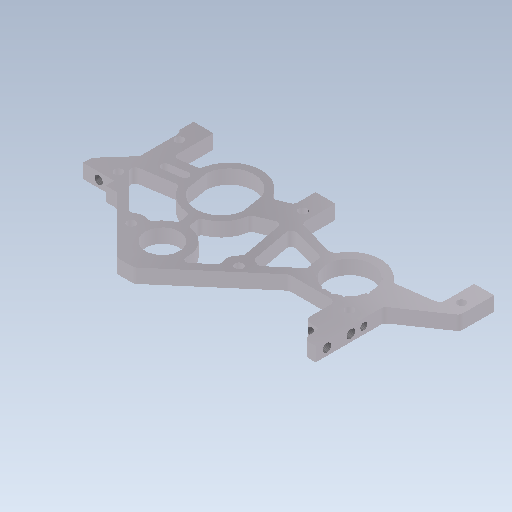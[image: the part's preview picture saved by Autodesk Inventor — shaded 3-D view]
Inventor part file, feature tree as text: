
AUTODESK INVENTOR PART (.ipt)
format: ipt  version: 2020 (Build 240168000, 168)  size: 420,864 bytes
history: native  units: mm
features: sketch x26, extrude x9, hole x9, thread x7, fillet x2, plane x1
ambient origin geometry x8: Origin, YZ Plane, XZ Plane, XY Plane, X Axis, Y Axis, Z Axis, Center Point
bodies: Solid1 (feature_tree)
feature tree (54):
  plane  "Work Plane1"
  extrude  "Extrude8"  Depth=5.0mm
  fillet  "Fillet1"  Radius=2.0mm
  extrude  "Extrude7"  Depth=2.0mm
  extrude  "Extrude6"  Depth=2.0mm
  extrude  "Extrude5"  Depth=2.0mm
  extrude  "Extrude4"  Depth=2.0mm
  extrude  "Extrude3"  Depth=1.5mm
  extrude  "Extrude2"  Depth=1.5mm
  extrude  "Extrude1"  Depth=2.0mm
  hole  "Hole8"  [1 undecoded]
  hole  "Hole7"  [1 undecoded]
  hole  "Hole6"  [1 undecoded]
  hole  "Hole5"  [1 undecoded]
  hole  "Hole4"  [1 undecoded]
  hole  "Hole3"  [1 undecoded]
  hole  "Hole2"  [1 undecoded]
  hole  "Hole1"  [1 undecoded]
  thread  "Thread1"  [1 undecoded]
  thread  "Thread2"  [1 undecoded]
  thread  "Thread3"  [1 undecoded]
  thread  "Thread4"  [1 undecoded]
  thread  "Thread5"  [1 undecoded]
  thread  "Thread6"  [1 undecoded]
  thread  "Thread7"  [1 undecoded]
  hole  "Hole23"  [1 undecoded]
  extrude  "Extrusion11"  [1 undecoded]
  fillet  "Fillet2"  [1 undecoded]
  sketch  "Sketch25"  dims[d99=3.0mm d100=6.0mm d101=4.0mm d102=2.0mm d103=90.0deg d104=8.0mm d105=20.594885mm]
  sketch  "Sketch1"  dims[d0=21.5mm d1=5.0mm d2=0.0mm d3=2.0mm]
  sketch  "Sketch2"  dims[d4=2.0mm d5=2.0mm]
  sketch  "Sketch3"  dims[d6=2.0mm d7=2.0mm]
  sketch  "Sketch4"  dims[d8=2.0mm d9=2.0mm]
  sketch  "Sketch5"  dims[d10=2.0mm d11=2.0mm]
  sketch  "Sketch6"  dims[d12=1.5mm d13=1.5mm]
  sketch  "Sketch7"  dims[d14=1.5mm d15=1.5mm]
  sketch  "Sketch8"  dims[d16=2.0mm d17=2.0mm]
  sketch  "Sketch9"  dims[d18=2.0mm d19=2.0mm]
  sketch  "Sketch10"  dims[d20=2.0mm d21=2.0mm]
  sketch  "Sketch11"  dims[d22=3.0mm d23=-0.0mm d24=5.0mm d25=-0.0mm]
  sketch  "Sketch12"  dims[d26=5.0mm d27=-0.0mm d28=5.0mm d29=-0.0mm]
  sketch  "Sketch13"  dims[d30=5.0mm d31=-0.0mm d32=5.0mm d33=-0.0mm]
  sketch  "Sketch14"  dims[d34=5.0mm d35=-0.0mm]
  sketch  "Sketch15"  dims[d36=3.0mm d37=6.0mm d38=4.0mm d39=2.0mm d40=90.0deg d41=6.0mm d42=20.594885mm]
  sketch  "Sketch16"  dims[d43=3.0mm d44=6.0mm d45=4.0mm d46=2.0mm d47=90.0deg d48=4.0mm d49=20.594885mm]
  sketch  "Sketch17"  dims[d50=3.0mm d51=6.0mm d52=4.0mm d53=2.0mm d54=90.0deg d55=8.0mm d56=20.594885mm]
  sketch  "Sketch18"  dims[d57=3.0mm d58=6.0mm d59=4.0mm d60=2.0mm d61=90.0deg d62=8.0mm d63=20.594885mm]
  sketch  "Sketch19"  dims[d64=3.0mm d65=6.0mm d66=4.0mm d67=2.0mm d68=90.0deg d69=8.0mm d70=20.594885mm]
  sketch  "Sketch20"  dims[d71=3.0mm d72=6.0mm d73=4.0mm d74=2.0mm d75=90.0deg d76=8.0mm d77=20.594885mm]
  sketch  "Sketch21"  dims[d78=3.0mm d79=6.0mm d80=4.0mm d81=2.0mm d82=90.0deg d83=8.0mm d84=20.594885mm]
  sketch  "Sketch22"  dims[d85=3.0mm d86=6.0mm d87=4.0mm d88=2.0mm d89=90.0deg d90=8.0mm d91=20.594885mm]
  sketch  "Sketch23"  dims[d92=3.0mm d93=6.0mm d94=4.0mm d95=2.0mm d96=90.0deg d97=8.0mm d98=20.594885mm]
  sketch  "Sketch26"  dims[d106=12.0mm d107=6.0mm d108=4.0mm d109=2.0mm d110=90.0deg d111=8.0mm d112=20.594885mm]
  sketch  "Sketch27"  dims[d113=3.0mm d114=6.0mm d115=4.0mm d116=2.0mm d117=90.0deg d118=8.0mm d119=20.594885mm d120=3.0mm d121=6.0mm d122=4.0mm d123=2.0mm d124=90.0deg d125=5.0mm d126=0.0mm d127=3.0mm d128=4.0mm d129=4.0mm d130=2.0mm d131=90.0deg d132=5.0mm d133=0.0mm d134=3.0mm d135=6.0mm d136=4.0mm d137=2.0mm d138=90.0deg d139=5.0mm d140=0.0mm d145=3.0mm d146=4.0mm d151=10.0mm d152=0.0mm d153=10.0mm d154=0.0mm d155=10.0mm d156=0.0mm d157=10.0mm d158=0.0mm d159=10.0mm d160=0.0mm d161=10.0mm d162=0.0mm d163=10.0mm d164=0.0mm d165=17.0mm d166=2.459mm d167=6.0mm d168=4.0mm d169=2.0mm d170=90.0deg d171=2.75mm d172=20.594885mm d173=1.0mm d174=0.0mm d175=2.0mm]
note: 18 required parameter values undecoded (feature->parameter linkage not recoverable at this tier; creation-order binding heuristic only, values carry confidence <= 0.55)
